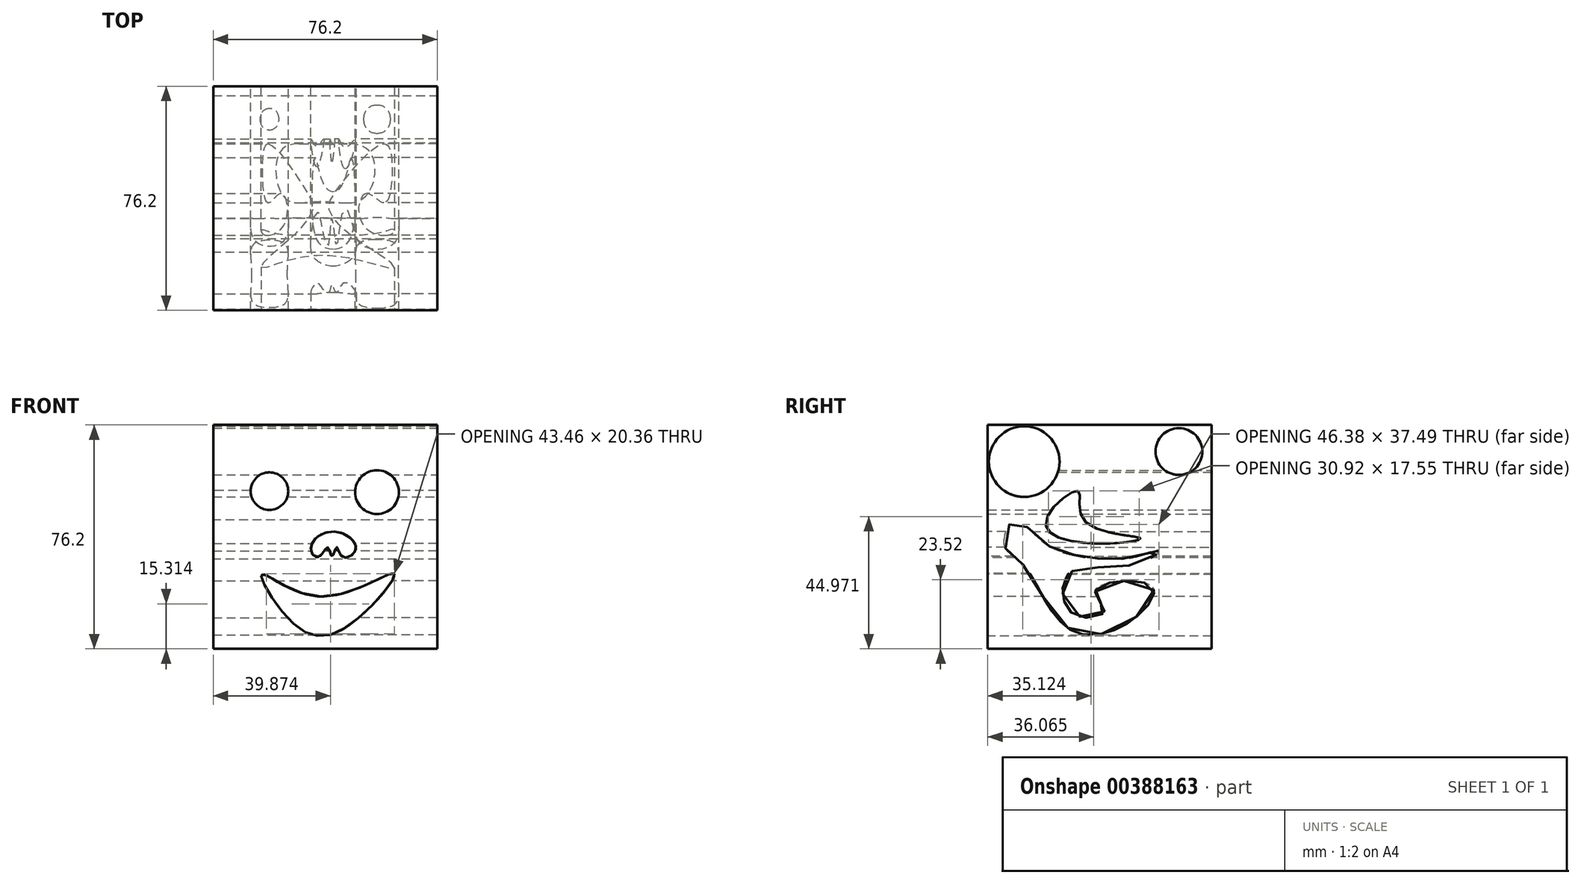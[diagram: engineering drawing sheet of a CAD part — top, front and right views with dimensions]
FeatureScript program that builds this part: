
annotation { "Feature Type Name" : "Feature", "Feature Type Description" : "" }
export const myFeature = defineFeature(function(context is Context, id is Id, definition is map)
    precondition{}
    {
        {
            var Q0;
            Q0=qCreatedBy(makeId("Front.planeOp"),FACE);
            var sketch = newSketch(context, id + "F0", { "sketchPlane" : qUnion([Q0])});
            skLineSegment(sketch, "E0.bottom", {"start": v(-40.96, 37.88) * mm, "end": v(35.24, 37.88) * mm});
            skLineSegment(sketch, "E0.top", {"start": v(-40.96, -38.32) * mm, "end": v(35.24, -38.32) * mm});
            skLineSegment(sketch, "E0.left", {"start": v(-40.96, 37.88) * mm, "end": v(-40.96, -38.32) * mm});
            skLineSegment(sketch, "E0.right", {"start": v(35.24, 37.88) * mm, "end": v(35.24, -38.32) * mm});
            skSolve(sketch);
        }
        {
            var Q0;
            Q0=makeQuery(id+"F0.imprint","IMPRINT",FACE,{"disambiguationData":[TD([[makeQuery(id+"F0.imprint","IMPRINT",EDGE,{"derivedFrom":sQuery(id+"F0.wireOp",EDGE,"E0.bottom")}),-1.0]])]});
            extrude(context, id + "F1", {"entities" : qUnion([Q0]), "depth" : 76.2 * mm});
        }
        {
            var Q0;
            Q0=makeQuery(id+"F1.opExtrude","CAP_FACE",FACE,{"disambiguationData":[OSD([sQuery(id+"F0.wireOp",EDGE,"E0.bottom"),sQuery(id+"F0.wireOp",EDGE,"E0.top"),sQuery(id+"F0.wireOp",EDGE,"E0.left"),sQuery(id+"F0.wireOp",EDGE,"E0.right")])],"isStart":true});
            var sketch = newSketch(context, id + "F2", { "sketchPlane" : qUnion([Q0])});
            skCircle(sketch, "E1", {"center": v(-14.77, 14.98) * mm, "radius": 7.45 * mm});
            skSolve(sketch);
        }
        {
            var Q0;
            Q0=makeQuery(id+"F2.imprint","IMPRINT",FACE,{"disambiguationData":[TD([[makeQuery(id+"F2.imprint","IMPRINT",EDGE,{"derivedFrom":sQuery(id+"F2.wireOp",EDGE,"E1")}),1.0]])]});
            extrude(context, id + "F3", {"entities" : qUnion([Q0]), "operationType" : NewBodyOperationType.REMOVE, "oppositeDirection" : true, "depth" : 171.2 * mm});
        }
        {
            var Q0;
            Q0=makeQuery(id+"F1.opExtrude","CAP_FACE",FACE,{"disambiguationData":[OSD([sQuery(id+"F0.wireOp",EDGE,"E0.bottom"),sQuery(id+"F0.wireOp",EDGE,"E0.top"),sQuery(id+"F0.wireOp",EDGE,"E0.left"),sQuery(id+"F0.wireOp",EDGE,"E0.right")])],"isStart":true});
            var sketch = newSketch(context, id + "F4", { "sketchPlane" : qUnion([Q0])});
            skCircle(sketch, "E2", {"center": v(21.82, 15.33) * mm, "radius": 6.4 * mm});
            skSolve(sketch);
        }
        {
            var Q0;
            Q0 = qSketchRegion(id + "F4", true);
            extrude(context, id + "F5", {"entities" : qUnion([Q0]), "operationType" : NewBodyOperationType.REMOVE, "oppositeDirection" : true, "depth" : 162.3 * mm});
        }
        {
            var Q0;
            Q0=makeQuery(id+"F1.opExtrude","CAP_FACE",FACE,{"disambiguationData":[OSD([sQuery(id+"F0.wireOp",EDGE,"E0.bottom"),sQuery(id+"F0.wireOp",EDGE,"E0.top"),sQuery(id+"F0.wireOp",EDGE,"E0.left"),sQuery(id+"F0.wireOp",EDGE,"E0.right")])],"isStart":true});
            var sketch = newSketch(context, id + "F6", { "sketchPlane" : qUnion([Q0])});
            skFitSpline(sketch, "E3", {"points": [v(-0.17, 1.59) * mm, v(-7.66, -4.3) * mm, v(-2.92, -7.04) * mm, v(-1.02, -3.72) * mm, v(0.59, -6.85) * mm, v(1.92, -3.82) * mm, v(5.23, -7.14) * mm, v(7.8, -3.82) * mm, v(-0.17, 1.59) * mm]});
            skSolve(sketch);
        }
        {
            var Q0;
            Q0 = qSketchRegion(id + "F6", true);
            extrude(context, id + "F7", {"entities" : qUnion([Q0]), "operationType" : NewBodyOperationType.REMOVE, "oppositeDirection" : true, "depth" : 197.1 * mm});
        }
        {
            var Q0;
            Q0=makeQuery(id+"F1.opExtrude","CAP_FACE",FACE,{"disambiguationData":[OSD([sQuery(id+"F0.wireOp",EDGE,"E0.bottom"),sQuery(id+"F0.wireOp",EDGE,"E0.top"),sQuery(id+"F0.wireOp",EDGE,"E0.left"),sQuery(id+"F0.wireOp",EDGE,"E0.right")])],"isStart":true});
            var sketch = newSketch(context, id + "F8", { "sketchPlane" : qUnion([Q0])});
            skFitSpline(sketch, "E4", {"points": [v(-20.65, -12.82) * mm, v(-3.87, -31.22) * mm, v(13.77, -29.7) * mm, v(24.48, -13.01) * mm, v(4.67, -20.5) * mm, v(-20.65, -12.82) * mm]});
            skSolve(sketch);
        }
        {
            var Q0;
            Q0 = qSketchRegion(id + "F8", true);
            extrude(context, id + "F9", {"entities" : qUnion([Q0]), "operationType" : NewBodyOperationType.REMOVE, "oppositeDirection" : true, "depth" : 207.26 * mm});
        }
        {
            var Q0;
            Q0=makeQuery(id+"F1.opExtrude","SWEPT_FACE",FACE,{"disambiguationData":[OSD([sQuery(id+"F0.wireOp",EDGE,"E0.right")])]});
            var sketch = newSketch(context, id + "F10", { "sketchPlane" : qUnion([Q0])});
            skCircle(sketch, "E5", {"center": v(-63.8, 25.38) * mm, "radius": 12.01 * mm});
            skSolve(sketch);
        }
        {
            var Q0;
            Q0 = qSketchRegion(id + "F10", true);
            extrude(context, id + "F11", {"entities" : qUnion([Q0]), "operationType" : NewBodyOperationType.REMOVE, "oppositeDirection" : true, "depth" : 238.76 * mm});
        }
        {
            var Q0;
            Q0=makeQuery(id+"F1.opExtrude","SWEPT_FACE",FACE,{"disambiguationData":[OSD([sQuery(id+"F0.wireOp",EDGE,"E0.right")])]});
            var sketch = newSketch(context, id + "F12", { "sketchPlane" : qUnion([Q0])});
            skCircle(sketch, "E6", {"center": v(-11.18, 28.8) * mm, "radius": 7.95 * mm});
            skSolve(sketch);
        }
        {
            var Q0;
            Q0 = qSketchRegion(id + "F12", true);
            extrude(context, id + "F13", {"entities" : qUnion([Q0]), "operationType" : NewBodyOperationType.REMOVE, "oppositeDirection" : true, "depth" : 197.87 * mm});
        }
        {
            var Q0;
            Q0=makeQuery(id+"F1.opExtrude","SWEPT_FACE",FACE,{"disambiguationData":[OSD([sQuery(id+"F0.wireOp",EDGE,"E0.right")])]});
            var sketch = newSketch(context, id + "F14", { "sketchPlane" : qUnion([Q0])});
            skFitSpline(sketch, "E7", {"points": [v(-45.5, 15.43) * mm, v(-56.5, 5) * mm, v(-41.32, -2.4) * mm, v(-24.35, -0.7) * mm, v(-43.6, 5.57) * mm, v(-45.5, 15.43) * mm]});
            skSolve(sketch);
        }
        {
            var Q0;
            Q0 = qSketchRegion(id + "F14", true);
            extrude(context, id + "F15", {"entities" : qUnion([Q0]), "operationType" : NewBodyOperationType.REMOVE, "oppositeDirection" : true, "depth" : 214.63 * mm});
        }
        {
            var Q0;
            Q0=makeQuery(id+"F1.opExtrude","SWEPT_FACE",FACE,{"disambiguationData":[OSD([sQuery(id+"F0.wireOp",EDGE,"E0.right")])]});
            var sketch = newSketch(context, id + "F16", { "sketchPlane" : qUnion([Q0])});
            skFitSpline(sketch, "E8", {"points": [v(-64.26, -9.6) * mm, v(-49.29, -31.03) * mm, v(-28.8, -29.7) * mm, v(-20.47, -17) * mm, v(-39.52, -18.32) * mm, v(-36.49, -25.43) * mm, v(-47.2, -26.38) * mm, v(-49.57, -13.87) * mm, v(-40.75, -10.64) * mm, v(-24.35, -9.03) * mm, v(-17.9, -5.15) * mm, v(-26.16, -6.95) * mm, v(-37.63, -7.7) * mm, v(-47.58, -6.19) * mm, v(-58.3, -1.26) * mm, v(-67.2, 5.38) * mm, v(-70.52, -3.06) * mm, v(-64.26, -9.6) * mm]});
            skSolve(sketch);
        }
        {
            var Q0;
            Q0 = qSketchRegion(id + "F16", true);
            extrude(context, id + "F17", {"entities" : qUnion([Q0]), "operationType" : NewBodyOperationType.REMOVE, "oppositeDirection" : true, "depth" : 249.68 * mm});
        }
    });
